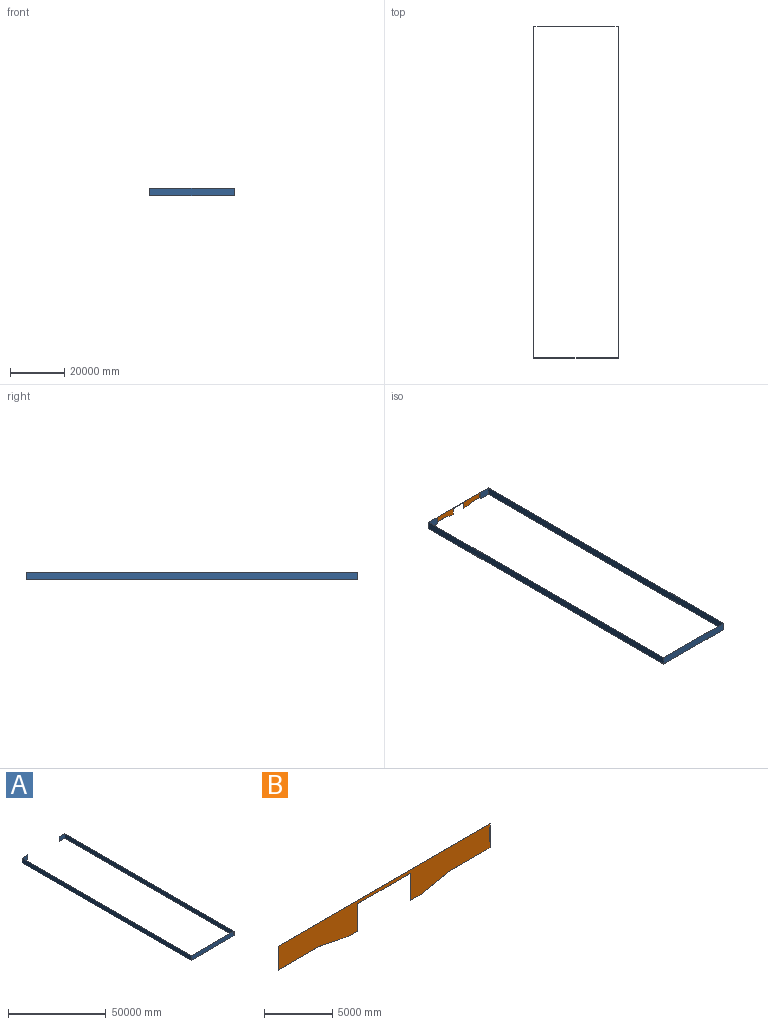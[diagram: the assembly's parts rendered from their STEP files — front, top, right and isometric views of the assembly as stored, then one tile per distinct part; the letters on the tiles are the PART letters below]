
ASSEMBLY  parts=2 mates=1
PART A: 14 faces, bbox 31115x122555x2895.6 mm
  f0: plane 4279.9x2895.6mm, normal (0,1,0), area 12392878.4mm2, adj f4,f5,f8,f13
  f1: plane 4279.9x2895.6mm, normal (0,1,0), area 12392878.4mm2, adj f4,f5,f6,f12
  f2: plane 4267.2x2895.6mm, normal (0,-1,0), area 12356104.3mm2, adj f4,f5,f9,f13
  f3: plane 4267.2x2895.6mm, normal (0,-1,0), area 12356104.3mm2, adj f4,f5,f11,f12
  f4: plane 122555x31115mm, normal (0,0,1), area 3616121.8mm2, adj f0,f1,f2,f3,f6,f7,f8,f9
  f5: plane 122555x31115mm, normal (0,0,-1), area 3616121.8mm2, adj f0,f1,f2,f3,f6,f7,f8,f9
  f6: plane 122555x2895.6mm, normal (-1,0,0), area 354870258mm2, adj f1,f4,f5,f7
  f7: plane 31115x2895.6mm, normal (0,-1,0), area 90096594mm2, adj f4,f5,f6,f8
  f8: plane 122555x2895.6mm, normal (1,0,0), area 354870258mm2, adj f0,f4,f5,f7
  f9: plane 122529.6x2895.6mm, normal (-1,0,0), area 354796709.8mm2, adj f2,f4,f5,f10
  f10: plane 31089.6x2895.6mm, normal (0,1,0), area 90023045.8mm2, adj f4,f5,f9,f11
  f11: plane 122529.6x2895.6mm, normal (1,0,0), area 354796709.8mm2, adj f3,f4,f5,f10
  f12: plane 2895.6x12.7mm, normal (1,0,0), area 36774.1mm2, adj f1,f3,f4,f5
  f13: plane 2895.6x12.7mm, normal (-1,0,0), area 36774.1mm2, adj f0,f2,f4,f5
PART B: 14 faces, bbox 21945.6x12.7x2743.2 mm
  f0: plane 5486.4x12.7mm, normal (0,0,-1), area 69677.3mm2, adj f1,f2,f3,f4
  f1: plane 21945.6x2743.2mm, normal (0,1,0), area 39855404.2mm2, adj f0,f3,f4,f5,f6,f7,f8,f9
  f2: plane 21945.6x2743.2mm, normal (0,-1,0), area 39855404.2mm2, adj f0,f3,f4,f5,f6,f7,f8,f9
  f3: plane 2438.4x12.7mm, normal (-1,0,0), area 30967.7mm2, adj f0,f1,f2,f9
  f4: plane 2438.4x12.7mm, normal (1,0,0), area 30967.7mm2, adj f0,f1,f2,f10
  f5: plane 21945.6x12.7mm, normal (0,0,1), area 278709.1mm2, adj f1,f2,f6,f13
  f6: plane 2133.6x12.7mm, normal (1,0,0), area 27096.7mm2, adj f1,f2,f5,f7
  f7: plane 4191x12.7mm, normal (0,0,-1), area 53225.7mm2, adj f1,f2,f6,f8
  f8: plane 3048x609.6mm, normal (0.2,0,-0.98), area 39476.2mm2, adj f1,f2,f7,f9
  f9: plane 990.6x12.7mm, normal (0,0,-1), area 12580.6mm2, adj f1,f2,f3,f8
  f10: plane 990.6x12.7mm, normal (0,0,-1), area 12580.6mm2, adj f1,f2,f4,f11
  f11: plane 3048x609.6mm, normal (-0.2,0,-0.98), area 39476.2mm2, adj f1,f2,f10,f12
  f12: plane 4191x12.7mm, normal (0,0,-1), area 53225.7mm2, adj f1,f2,f11,f13
  f13: plane 2133.6x12.7mm, normal (-1,0,0), area 27096.7mm2, adj f1,f2,f5,f12
PLACE A at identity
PLACE B at identity fixed
MATE fastened B.f5 <-> A.f4  axis (0,0,1) through (11277.6,61277.5,2895.6)mm
